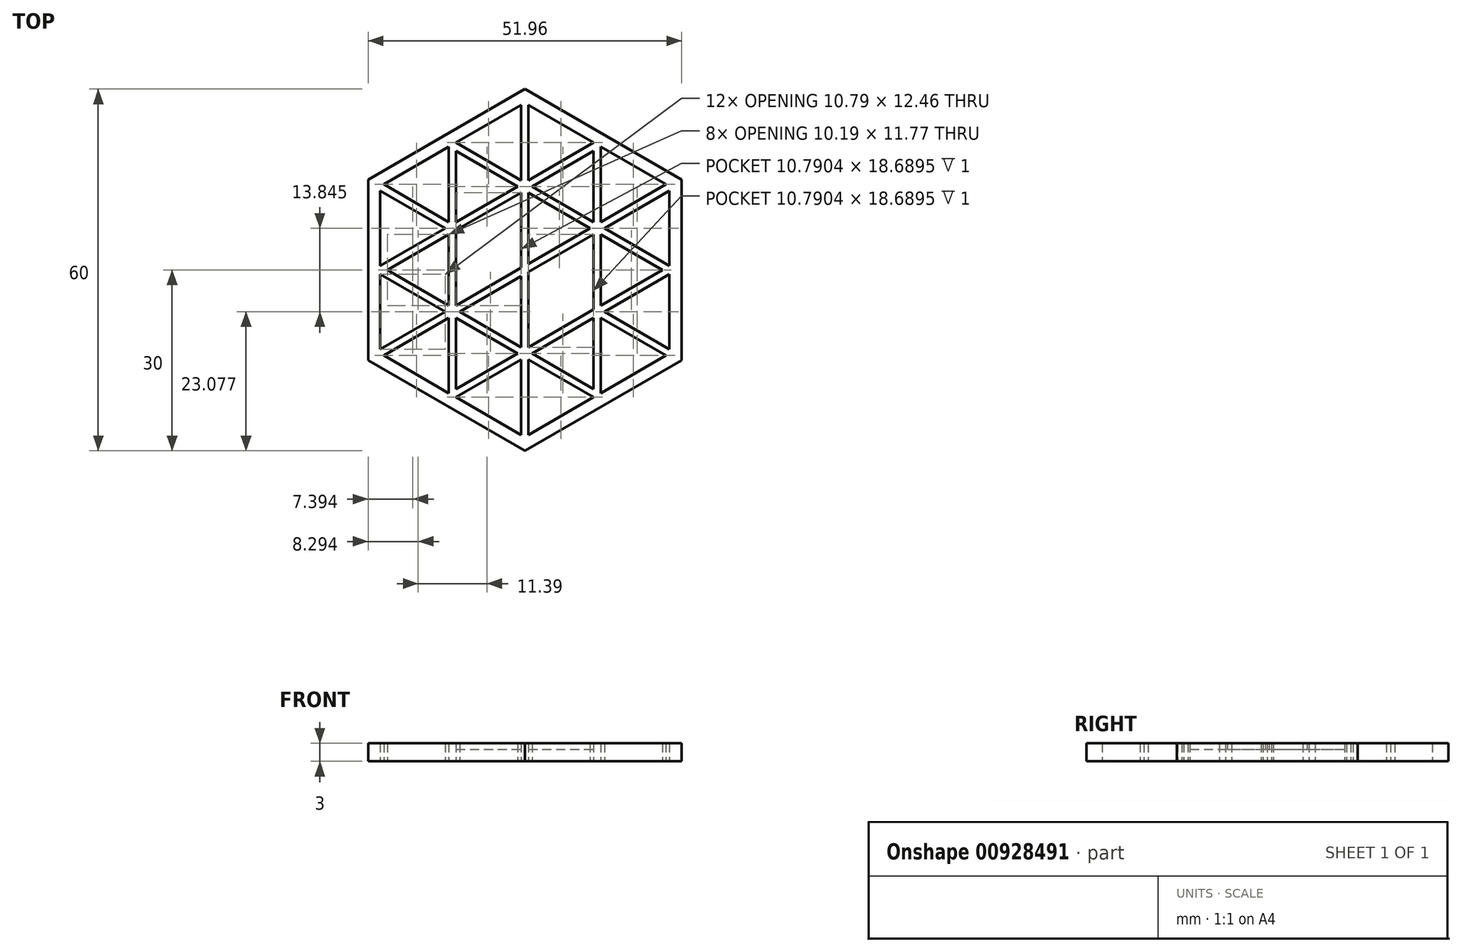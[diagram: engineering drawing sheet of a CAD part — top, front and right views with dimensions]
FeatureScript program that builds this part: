
annotation { "Feature Type Name" : "Feature", "Feature Type Description" : "" }
export const myFeature = defineFeature(function(context is Context, id is Id, definition is map)
    precondition{}
    {
        {
            var Q0;
            Q0=qCreatedBy(makeId("Top.planeOp"),FACE);
            var sketch = newSketch(context, id + "F0", { "sketchPlane" : qUnion([Q0])});
            skCircle(sketch, "E0.cCircle", {"center": v(0, 0) * mm, "radius": 30 * mm, "construction": true});
            skLineSegment(sketch, "E0.0", {"start": v(0, 30) * mm, "end": v(25.98, 15) * mm});
            skLineSegment(sketch, "E0.1", {"start": v(25.98, 15) * mm, "end": v(25.98, -15) * mm});
            skLineSegment(sketch, "E0.2", {"start": v(25.98, -15) * mm, "end": v(0, -30) * mm});
            skLineSegment(sketch, "E0.3", {"start": v(0, -30) * mm, "end": v(-25.98, -15) * mm});
            skLineSegment(sketch, "E0.4", {"start": v(-25.98, -15) * mm, "end": v(-25.98, 15) * mm});
            skLineSegment(sketch, "E0.5", {"start": v(-25.98, 15) * mm, "end": v(0, 30) * mm});
            skArc(sketch, "E1.cCircle", {"start": v(23.68, 14.36) * mm, "mid": v(-23.98, -13.85) * mm, "end": v(24.28, 13.32) * mm, "construction": true});
            skLineSegment(sketch, "E1.0", {"start": v(0.6, 27.34) * mm, "end": v(23.38, 14.2) * mm});
            skLineSegment(sketch, "E1.1", {"start": v(23.98, 13.15) * mm, "end": v(23.98, 0.7) * mm});
            skLineSegment(sketch, "E1.2", {"start": v(23.38, -14.2) * mm, "end": v(12.6, -20.42) * mm});
            skLineSegment(sketch, "E1.3", {"start": v(-0.6, -27.34) * mm, "end": v(-11.4, -21.11) * mm});
            skLineSegment(sketch, "E1.4", {"start": v(-23.98, -13.15) * mm, "end": v(-23.98, -0.7) * mm});
            skLineSegment(sketch, "E1.5", {"start": v(-23.38, 14.2) * mm, "end": v(-12.6, 20.42) * mm});
            skLineSegment(sketch, "E2", {"start": v(-23.98, -13.85) * mm, "end": v(23.98, 13.85) * mm, "construction": true});
            skLineSegment(sketch, "E3", {"start": v(-23.98, 0) * mm, "end": v(12, 20.77) * mm, "construction": true});
            skLineSegment(sketch, "E4", {"start": v(-12, -20.77) * mm, "end": v(23.98, 0) * mm, "construction": true});
            skLineSegment(sketch, "E5", {"start": v(0, -27.7) * mm, "end": v(0, 27.7) * mm, "construction": true});
            skLineSegment(sketch, "E6", {"start": v(-12, -20.77) * mm, "end": v(-12, 20.77) * mm, "construction": true});
            skLineSegment(sketch, "E7", {"start": v(12, -20.77) * mm, "end": v(12, 20.77) * mm, "construction": true});
            skLineSegment(sketch, "E8", {"start": v(23.98, -13.85) * mm, "end": v(-23.98, 13.85) * mm, "construction": true});
            skLineSegment(sketch, "E9", {"start": v(12, -20.77) * mm, "end": v(-23.98, 0) * mm, "construction": true});
            skLineSegment(sketch, "E10", {"start": v(23.98, 0) * mm, "end": v(-12, 20.77) * mm, "construction": true});
            skLineSegment(sketch, "E11.0", {"start": v(12.6, -20.42) * mm, "end": v(12.6, -7.96) * mm});
            skLineSegment(sketch, "E12.0", {"start": v(0.6, -27.7) * mm, "end": v(0.6, -27.68) * mm});
            skLineSegment(sketch, "E13.0", {"start": v(-0.6, -27.7) * mm, "end": v(-0.6, -27.68) * mm});
            skLineSegment(sketch, "E14.0", {"start": v(-12.6, -20.42) * mm, "end": v(-12.6, -7.96) * mm});
            skLineSegment(sketch, "E15.0", {"start": v(-11.4, -21.11) * mm, "end": v(-0.6, -14.88) * mm});
            skLineSegment(sketch, "E16.0", {"start": v(-23.68, -14.36) * mm, "end": v(-23.68, -14.36) * mm});
            skLineSegment(sketch, "E17.0", {"start": v(-22.78, 0) * mm, "end": v(-12.6, 5.88) * mm});
            skLineSegment(sketch, "E18.0", {"start": v(-23.98, 0.7) * mm, "end": v(-13.2, 6.92) * mm});
            skLineSegment(sketch, "E19.0", {"start": v(-24.28, -13.33) * mm, "end": v(-24.28, -13.32) * mm});
            skLineSegment(sketch, "E20.0", {"start": v(-11.4, -19.73) * mm, "end": v(-1.2, -13.85) * mm});
            skLineSegment(sketch, "E21.0", {"start": v(23.98, 0.7) * mm, "end": v(13.2, 6.92) * mm});
            skLineSegment(sketch, "E22.0", {"start": v(24.28, -13.33) * mm, "end": v(24.28, -13.32) * mm});
            skLineSegment(sketch, "E23.0", {"start": v(23.68, -14.36) * mm, "end": v(23.68, -14.36) * mm});
            skLineSegment(sketch, "E24.0", {"start": v(11.4, -21.11) * mm, "end": v(0.6, -14.88) * mm});
            skLineSegment(sketch, "E25.trimOffspring", {"start": v(23.68, 14.36) * mm, "end": v(23.68, 14.36) * mm});
            skLineSegment(sketch, "E26.trimOffspring", {"start": v(24.28, 13.32) * mm, "end": v(24.28, 13.33) * mm});
            skLineSegment(sketch, "E27.trimOffspring", {"start": v(23.98, -0.7) * mm, "end": v(23.98, -13.15) * mm});
            skLineSegment(sketch, "E28.trimOffspring", {"start": v(22.78, 0) * mm, "end": v(12.6, 5.88) * mm});
            skLineSegment(sketch, "E29.trimOffspring", {"start": v(23.38, -14.2) * mm, "end": v(12.6, -7.96) * mm});
            skLineSegment(sketch, "E30.trimOffspring", {"start": v(23.98, -13.15) * mm, "end": v(13.2, -6.92) * mm});
            skLineSegment(sketch, "E31.trimOffspring", {"start": v(11.4, -21.11) * mm, "end": v(0.6, -27.34) * mm});
            skLineSegment(sketch, "E32.trimOffspring", {"start": v(11.4, -19.73) * mm, "end": v(11.4, -7.96) * mm});
            skLineSegment(sketch, "E33.trimOffspring", {"start": v(11.4, -19.73) * mm, "end": v(1.2, -13.85) * mm});
            skLineSegment(sketch, "E34.trimOffspring", {"start": v(0.6, -27.34) * mm, "end": v(0.6, -14.88) * mm});
            skLineSegment(sketch, "E35.trimOffspring", {"start": v(-0.6, -27.34) * mm, "end": v(-0.6, -14.88) * mm});
            skLineSegment(sketch, "E36.trimOffspring", {"start": v(-12.6, -20.42) * mm, "end": v(-23.38, -14.2) * mm});
            skLineSegment(sketch, "E37.trimOffspring", {"start": v(-11.4, -19.73) * mm, "end": v(-11.4, -7.96) * mm});
            skLineSegment(sketch, "E38.trimOffspring", {"start": v(-23.98, -13.15) * mm, "end": v(-13.2, -6.92) * mm});
            skLineSegment(sketch, "E39.trimOffspring", {"start": v(-23.38, -14.2) * mm, "end": v(-12.6, -7.96) * mm});
            skLineSegment(sketch, "E40.trimOffspring", {"start": v(-23.98, 0.7) * mm, "end": v(-23.98, 13.15) * mm});
            skLineSegment(sketch, "E41.trimOffspring", {"start": v(-23.68, 14.36) * mm, "end": v(-23.68, 14.36) * mm});
            skLineSegment(sketch, "E42.trimOffspring", {"start": v(-24.28, 13.32) * mm, "end": v(-24.28, 13.33) * mm});
            skLineSegment(sketch, "E43.trimOffspring", {"start": v(-11.4, 21.11) * mm, "end": v(-0.6, 27.34) * mm});
            skLineSegment(sketch, "E44.trimOffspring", {"start": v(-0.6, 27.68) * mm, "end": v(-0.6, 27.7) * mm});
            skLineSegment(sketch, "E45.trimOffspring", {"start": v(0.6, 27.68) * mm, "end": v(0.6, 27.7) * mm});
            skLineSegment(sketch, "E46.trimOffspring", {"start": v(12.6, 7.96) * mm, "end": v(12.6, 20.42) * mm});
            skLineSegment(sketch, "E47.trimOffspring", {"start": v(13.2, 6.92) * mm, "end": v(23.98, 13.15) * mm});
            skLineSegment(sketch, "E48.trimOffspring", {"start": v(10.8, 6.92) * mm, "end": v(0.6, 12.8) * mm});
            skLineSegment(sketch, "E49.trimOffspring", {"start": v(11.4, 7.96) * mm, "end": v(11.4, 19.73) * mm});
            skLineSegment(sketch, "E50.trimOffspring", {"start": v(12.6, 7.96) * mm, "end": v(23.38, 14.2) * mm});
            skLineSegment(sketch, "E51.trimOffspring", {"start": v(11.4, 7.96) * mm, "end": v(1.2, 13.85) * mm});
            skLineSegment(sketch, "E52.trimOffspring", {"start": v(1.2, 13.85) * mm, "end": v(11.4, 19.73) * mm});
            skLineSegment(sketch, "E53.trimOffspring", {"start": v(-0.6, 14.88) * mm, "end": v(-11.4, 21.11) * mm});
            skLineSegment(sketch, "E54.trimOffspring", {"start": v(0.6, 14.88) * mm, "end": v(11.4, 21.11) * mm});
            skLineSegment(sketch, "E55.trimOffspring", {"start": v(-1.2, 13.85) * mm, "end": v(-11.4, 19.73) * mm});
            skLineSegment(sketch, "E56.trimOffspring", {"start": v(-0.6, 14.88) * mm, "end": v(-0.6, 27.34) * mm});
            skLineSegment(sketch, "E57.trimOffspring", {"start": v(0.6, 14.88) * mm, "end": v(0.6, 27.34) * mm});
            skLineSegment(sketch, "E58.trimOffspring", {"start": v(-13.2, 6.92) * mm, "end": v(-23.98, 13.15) * mm});
            skLineSegment(sketch, "E59.trimOffspring", {"start": v(-12.6, 7.96) * mm, "end": v(-23.38, 14.2) * mm});
            skLineSegment(sketch, "E60.trimOffspring", {"start": v(0.6, 1.04) * mm, "end": v(0.6, 12.8) * mm});
            skLineSegment(sketch, "E61.trimOffspring", {"start": v(0.6, 1.04) * mm, "end": v(10.8, 6.92) * mm});
            skLineSegment(sketch, "E62.trimOffspring", {"start": v(-0.6, 0.35) * mm, "end": v(-0.6, 12.8) * mm});
            skLineSegment(sketch, "E63.trimOffspring", {"start": v(0.6, -0.35) * mm, "end": v(11.4, 5.88) * mm});
            skLineSegment(sketch, "E64.trimOffspring", {"start": v(12.6, -5.88) * mm, "end": v(22.78, 0) * mm});
            skLineSegment(sketch, "E65.trimOffspring", {"start": v(12.6, -5.88) * mm, "end": v(12.6, 5.88) * mm});
            skLineSegment(sketch, "E66.trimOffspring", {"start": v(13.2, -6.92) * mm, "end": v(23.98, -0.7) * mm});
            skLineSegment(sketch, "E67.trimOffspring", {"start": v(11.4, -6.58) * mm, "end": v(11.4, 5.88) * mm});
            skLineSegment(sketch, "E68.trimOffspring", {"start": v(0.6, -12.8) * mm, "end": v(11.4, -6.58) * mm});
            skLineSegment(sketch, "E69.trimOffspring", {"start": v(-0.6, -12.8) * mm, "end": v(-10.8, -6.92) * mm});
            skLineSegment(sketch, "E70.trimOffspring", {"start": v(0.6, -12.8) * mm, "end": v(0.6, -0.35) * mm});
            skLineSegment(sketch, "E71.trimOffspring", {"start": v(1.2, -13.85) * mm, "end": v(11.4, -7.96) * mm});
            skLineSegment(sketch, "E72.trimOffspring", {"start": v(-0.6, -12.8) * mm, "end": v(-0.6, -1.04) * mm});
            skLineSegment(sketch, "E73.trimOffspring", {"start": v(-1.2, -13.85) * mm, "end": v(-11.4, -7.96) * mm});
            skLineSegment(sketch, "E74.trimOffspring", {"start": v(-12.6, -5.88) * mm, "end": v(-22.78, 0) * mm});
            skLineSegment(sketch, "E75.trimOffspring", {"start": v(-12.6, -5.88) * mm, "end": v(-12.6, 5.88) * mm});
            skLineSegment(sketch, "E76.trimOffspring", {"start": v(-11.4, -5.88) * mm, "end": v(-0.6, 0.35) * mm});
            skLineSegment(sketch, "E77.trimOffspring", {"start": v(-11.4, -5.88) * mm, "end": v(-11.4, 6.58) * mm});
            skLineSegment(sketch, "E78.trimOffspring", {"start": v(-10.8, -6.92) * mm, "end": v(-0.6, -1.04) * mm});
            skLineSegment(sketch, "E79.trimOffspring", {"start": v(-13.2, -6.92) * mm, "end": v(-23.98, -0.7) * mm});
            skLineSegment(sketch, "E80.trimOffspring", {"start": v(-11.4, 6.58) * mm, "end": v(-0.6, 12.8) * mm});
            skLineSegment(sketch, "E81.trimOffspring", {"start": v(-11.4, 7.96) * mm, "end": v(-11.4, 19.73) * mm});
            skLineSegment(sketch, "E82.trimOffspring", {"start": v(-11.4, 7.96) * mm, "end": v(-1.2, 13.85) * mm});
            skLineSegment(sketch, "E83.trimOffspring", {"start": v(-12.6, 7.96) * mm, "end": v(-12.6, 20.42) * mm});
            skSolve(sketch);
        }
        {
            var Q0;
            Q0 = qSketchRegion(id + "F0", true);
            extrude(context, id + "F1", {"entities" : qUnion([Q0]), "flatOperationType" : FlatOperationType.REMOVE, "depth" : 3 * mm, "offsetDistance" : 25 * mm, "domain" : OperationDomain.MODEL});
        }
        {
            var Q0;
            Q0=makeQuery(id+"F1.opExtrude","CAP_FACE",FACE,{"disambiguationData":[OSD([sQuery(id+"F0.wireOp",EDGE,"E0.0"),sQuery(id+"F0.wireOp",EDGE,"E0.1"),sQuery(id+"F0.wireOp",EDGE,"E0.2"),sQuery(id+"F0.wireOp",EDGE,"E0.3"),sQuery(id+"F0.wireOp",EDGE,"E0.4"),sQuery(id+"F0.wireOp",EDGE,"E0.5"),sQuery(id+"F0.wireOp",EDGE,"E1.0"),sQuery(id+"F0.wireOp",EDGE,"E1.1"),sQuery(id+"F0.wireOp",EDGE,"E1.2"),sQuery(id+"F0.wireOp",EDGE,"E1.3"),sQuery(id+"F0.wireOp",EDGE,"E1.4"),sQuery(id+"F0.wireOp",EDGE,"E1.5"),sQuery(id+"F0.wireOp",EDGE,"E11.0"),sQuery(id+"F0.wireOp",EDGE,"E14.0"),sQuery(id+"F0.wireOp",EDGE,"E15.0"),sQuery(id+"F0.wireOp",EDGE,"E17.0"),sQuery(id+"F0.wireOp",EDGE,"E18.0"),sQuery(id+"F0.wireOp",EDGE,"E20.0"),sQuery(id+"F0.wireOp",EDGE,"E21.0"),sQuery(id+"F0.wireOp",EDGE,"E24.0"),sQuery(id+"F0.wireOp",EDGE,"E27.trimOffspring"),sQuery(id+"F0.wireOp",EDGE,"E28.trimOffspring"),sQuery(id+"F0.wireOp",EDGE,"E29.trimOffspring"),sQuery(id+"F0.wireOp",EDGE,"E30.trimOffspring"),sQuery(id+"F0.wireOp",EDGE,"E31.trimOffspring"),sQuery(id+"F0.wireOp",EDGE,"E32.trimOffspring"),sQuery(id+"F0.wireOp",EDGE,"E33.trimOffspring"),sQuery(id+"F0.wireOp",EDGE,"E34.trimOffspring"),sQuery(id+"F0.wireOp",EDGE,"E35.trimOffspring"),sQuery(id+"F0.wireOp",EDGE,"E36.trimOffspring"),sQuery(id+"F0.wireOp",EDGE,"E37.trimOffspring"),sQuery(id+"F0.wireOp",EDGE,"E38.trimOffspring"),sQuery(id+"F0.wireOp",EDGE,"E39.trimOffspring"),sQuery(id+"F0.wireOp",EDGE,"E40.trimOffspring"),sQuery(id+"F0.wireOp",EDGE,"E43.trimOffspring"),sQuery(id+"F0.wireOp",EDGE,"E46.trimOffspring"),sQuery(id+"F0.wireOp",EDGE,"E47.trimOffspring"),sQuery(id+"F0.wireOp",EDGE,"E48.trimOffspring"),sQuery(id+"F0.wireOp",EDGE,"E49.trimOffspring"),sQuery(id+"F0.wireOp",EDGE,"E50.trimOffspring"),sQuery(id+"F0.wireOp",EDGE,"E51.trimOffspring"),sQuery(id+"F0.wireOp",EDGE,"E52.trimOffspring"),sQuery(id+"F0.wireOp",EDGE,"E53.trimOffspring"),sQuery(id+"F0.wireOp",EDGE,"E54.trimOffspring"),sQuery(id+"F0.wireOp",EDGE,"E55.trimOffspring"),sQuery(id+"F0.wireOp",EDGE,"E56.trimOffspring"),sQuery(id+"F0.wireOp",EDGE,"E57.trimOffspring"),sQuery(id+"F0.wireOp",EDGE,"E58.trimOffspring"),sQuery(id+"F0.wireOp",EDGE,"E59.trimOffspring"),sQuery(id+"F0.wireOp",EDGE,"E60.trimOffspring"),sQuery(id+"F0.wireOp",EDGE,"E61.trimOffspring"),sQuery(id+"F0.wireOp",EDGE,"E62.trimOffspring"),sQuery(id+"F0.wireOp",EDGE,"E63.trimOffspring"),sQuery(id+"F0.wireOp",EDGE,"E64.trimOffspring"),sQuery(id+"F0.wireOp",EDGE,"E65.trimOffspring"),sQuery(id+"F0.wireOp",EDGE,"E66.trimOffspring"),sQuery(id+"F0.wireOp",EDGE,"E67.trimOffspring"),sQuery(id+"F0.wireOp",EDGE,"E68.trimOffspring"),sQuery(id+"F0.wireOp",EDGE,"E69.trimOffspring"),sQuery(id+"F0.wireOp",EDGE,"E70.trimOffspring"),sQuery(id+"F0.wireOp",EDGE,"E71.trimOffspring"),sQuery(id+"F0.wireOp",EDGE,"E72.trimOffspring"),sQuery(id+"F0.wireOp",EDGE,"E73.trimOffspring"),sQuery(id+"F0.wireOp",EDGE,"E74.trimOffspring"),sQuery(id+"F0.wireOp",EDGE,"E75.trimOffspring"),sQuery(id+"F0.wireOp",EDGE,"E76.trimOffspring"),sQuery(id+"F0.wireOp",EDGE,"E77.trimOffspring"),sQuery(id+"F0.wireOp",EDGE,"E78.trimOffspring"),sQuery(id+"F0.wireOp",EDGE,"E79.trimOffspring"),sQuery(id+"F0.wireOp",EDGE,"E80.trimOffspring"),sQuery(id+"F0.wireOp",EDGE,"E81.trimOffspring"),sQuery(id+"F0.wireOp",EDGE,"E82.trimOffspring"),sQuery(id+"F0.wireOp",EDGE,"E83.trimOffspring")])],"isStart":true});
            var sketch = newSketch(context, id + "F2", { "sketchPlane" : qUnion([Q0])});
            skLineSegment(sketch, "E84", {"start": v(-0.6, -12.8) * mm, "end": v(-0.6, -0.35) * mm});
            skLineSegment(sketch, "E85", {"start": v(-0.6, -0.35) * mm, "end": v(-11.4, 5.88) * mm});
            skLineSegment(sketch, "E86", {"start": v(-11.4, 5.88) * mm, "end": v(-11.4, -6.58) * mm});
            skLineSegment(sketch, "E87", {"start": v(-11.4, -6.58) * mm, "end": v(-0.6, -12.8) * mm});
            skLineSegment(sketch, "E88", {"start": v(11.4, -5.88) * mm, "end": v(11.4, 6.58) * mm});
            skLineSegment(sketch, "E89", {"start": v(11.4, 6.58) * mm, "end": v(0.6, 12.8) * mm});
            skLineSegment(sketch, "E90", {"start": v(0.6, 12.8) * mm, "end": v(0.6, 0.35) * mm});
            skLineSegment(sketch, "E91", {"start": v(0.6, 0.35) * mm, "end": v(11.4, -5.88) * mm});
            skSolve(sketch);
        }
        {
            var Q0;
            Q0 = qSketchRegion(id + "F2", true);
            extrude(context, id + "F3", {"entities" : qUnion([Q0]), "operationType" : NewBodyOperationType.ADD, "flatOperationType" : FlatOperationType.REMOVE, "oppositeDirection" : true, "depth" : 2 * mm, "offsetDistance" : 25 * mm, "domain" : OperationDomain.MODEL});
        }
    });
